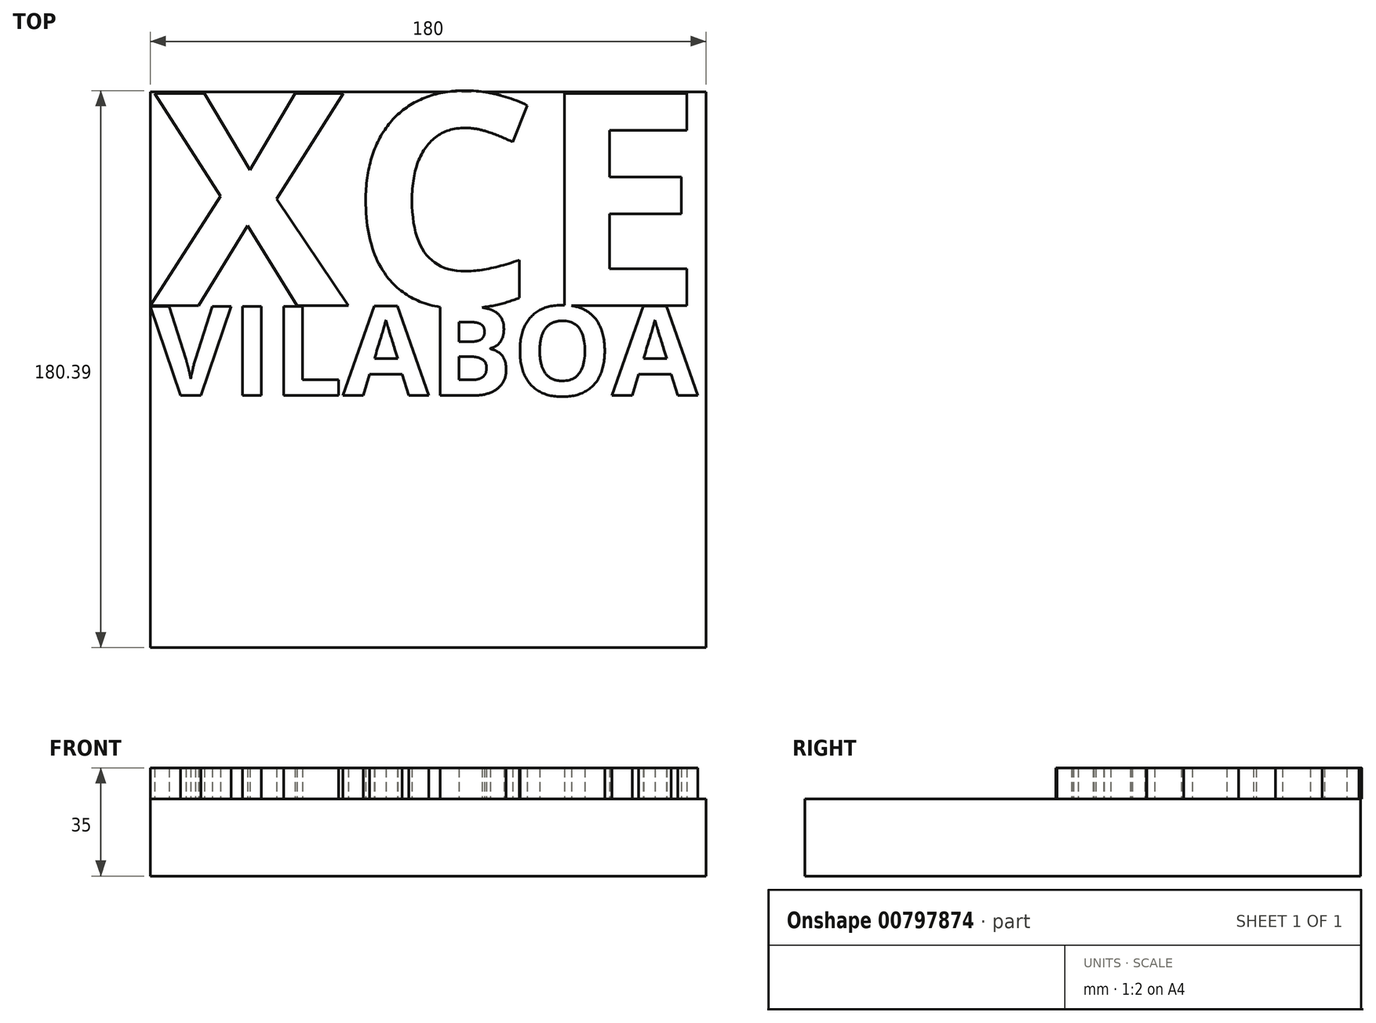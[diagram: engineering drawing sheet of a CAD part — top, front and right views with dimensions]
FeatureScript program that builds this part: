
annotation { "Feature Type Name" : "Feature", "Feature Type Description" : "" }
export const myFeature = defineFeature(function(context is Context, id is Id, definition is map)
    precondition{}
    {
        {
            var Q0;
            Q0=qCreatedBy(makeId("Top.planeOp"),FACE);
            var sketch = newSketch(context, id + "F0", { "sketchPlane" : qUnion([Q0])});
            skLineSegment(sketch, "E0.bottom", {"start": v(-90, 90) * mm, "end": v(90, 90) * mm});
            skLineSegment(sketch, "E0.top", {"start": v(-90, -90) * mm, "end": v(90, -90) * mm});
            skLineSegment(sketch, "E0.left", {"start": v(-90, 90) * mm, "end": v(-90, -90) * mm});
            skLineSegment(sketch, "E0.right", {"start": v(90, 90) * mm, "end": v(90, -90) * mm});
            skSolve(sketch);
        }
        {
            var Q0;
            Q0 = qSketchRegion(id + "F0", true);
            extrude(context, id + "F1", {"entities" : qUnion([Q0]), "depth" : 25 * mm, "offsetDistance" : 25 * mm});
        }
        {
            var Q0;
            Q0=makeQuery(id+"F1.opExtrude","CAP_FACE",FACE,{"disambiguationData":[OSD([sQuery(id+"F0.wireOp",EDGE,"E0.bottom"),sQuery(id+"F0.wireOp",EDGE,"E0.top"),sQuery(id+"F0.wireOp",EDGE,"E0.left"),sQuery(id+"F0.wireOp",EDGE,"E0.right")])],"isStart":false});
            var sketch = newSketch(context, id + "F2", { "sketchPlane" : qUnion([Q0])});
            skText(sketch, "E1", { "text": "XCE", "fontName": "OpenSans-Bold.ttf"});
            const initialGuessF2  = {"E1": [-0.09, 0.0207, 1, 0, 0.0693]};
            skSetInitialGuess(sketch, initialGuessF2);
            skSolve(sketch);
        }
        {
            var Q0;
            Q0 = qSketchRegion(id + "F2", true);
            extrude(context, id + "F3", {"entities" : qUnion([Q0]), "operationType" : NewBodyOperationType.ADD, "depth" : 10 * mm, "offsetDistance" : 25 * mm});
        }
        {
            var Q0;
            Q0=makeQuery(id+"F1.opExtrude","CAP_FACE",FACE,{"disambiguationData":[OSD([sQuery(id+"F0.wireOp",EDGE,"E0.bottom"),sQuery(id+"F0.wireOp",EDGE,"E0.top"),sQuery(id+"F0.wireOp",EDGE,"E0.left"),sQuery(id+"F0.wireOp",EDGE,"E0.right")])],"isStart":false});
            var sketch = newSketch(context, id + "F4", { "sketchPlane" : qUnion([Q0])});
            skText(sketch, "E2", { "text": "VILABOA", "fontName": "OpenSans-Bold.ttf"});
            const initialGuessF4  = {"E2": [-0.09, -0.00837, 1, 0, 0.02907]};
            skSetInitialGuess(sketch, initialGuessF4);
            skSolve(sketch);
        }
        {
            var Q0;
            Q0 = qSketchRegion(id + "F4", true);
            extrude(context, id + "F5", {"entities" : qUnion([Q0]), "operationType" : NewBodyOperationType.ADD, "depth" : 10 * mm, "offsetDistance" : 25 * mm});
        }
    });
